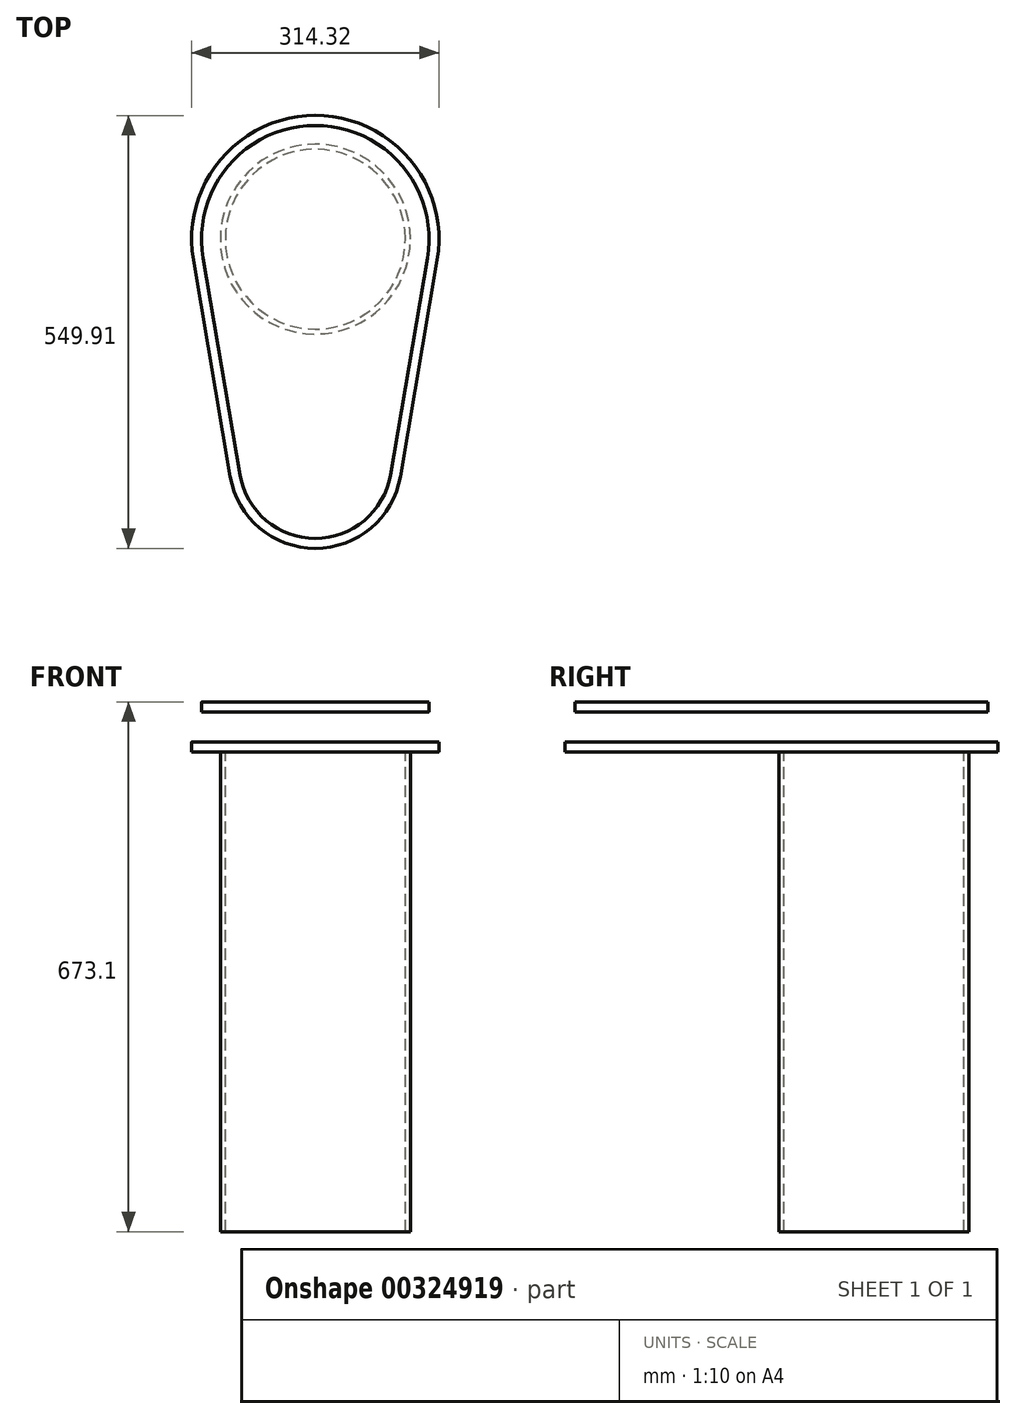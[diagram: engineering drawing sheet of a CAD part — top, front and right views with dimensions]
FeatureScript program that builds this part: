
annotation { "Feature Type Name" : "Feature", "Feature Type Description" : "" }
export const myFeature = defineFeature(function(context is Context, id is Id, definition is map)
    precondition{}
    {
        {
            var Q0;
            Q0=qCreatedBy(makeId("Top.planeOp"),FACE);
            var sketch = newSketch(context, id + "F0", { "sketchPlane" : qUnion([Q0])});
            skArc(sketch, "E0", {"start": v(142.4, -24.3) * mm, "mid": v(0, 144.46) * mm, "end": v(-142.4, -24.3) * mm});
            skArc(sketch, "E1", {"start": v(-95.46, -299.5) * mm, "mid": v(0, -380.05) * mm, "end": v(95.46, -299.5) * mm});
            skLineSegment(sketch, "E2", {"start": v(-142.4, -24.3) * mm, "end": v(-95.46, -299.5) * mm});
            skLineSegment(sketch, "E3", {"start": v(142.4, -24.3) * mm, "end": v(95.46, -299.5) * mm});
            skSolve(sketch);
        }
        {
            var Q0;
            Q0=qCreatedBy(makeId("Top.planeOp"),FACE);
            cPlane(context, id + "F1", {"entities" : qUnion([Q0]), "cplaneType" : CPlaneType.OFFSET, "offset" : 50.8 * mm, "oppositeDirection" : true, "width" : 152.4 * mm, "height" : 152.4 * mm});
        }
        {
            var Q0;
            Q0=qCreatedBy(id+"F1.planeOp",FACE);
            var sketch = newSketch(context, id + "F2", { "sketchPlane" : qUnion([Q0])});
            skLineSegment(sketch, "E4.0", {"start": v(-154.92, -26.43) * mm, "end": v(-107.98, -301.63) * mm});
            skArc(sketch, "E4.1", {"start": v(154.92, -26.43) * mm, "mid": v(0, 157.16) * mm, "end": v(-154.92, -26.43) * mm});
            skLineSegment(sketch, "E4.2", {"start": v(154.92, -26.43) * mm, "end": v(107.98, -301.63) * mm});
            skArc(sketch, "E4.3", {"start": v(-107.98, -301.63) * mm, "mid": v(0, -392.75) * mm, "end": v(107.98, -301.63) * mm});
            skSolve(sketch);
        }
        {
            var Q0;
            Q0=makeQuery(id+"F0.imprint","IMPRINT",FACE,{"disambiguationData":[TD([[makeQuery(id+"F0.imprint","IMPRINT",EDGE,{"derivedFrom":sQuery(id+"F0.wireOp",EDGE,"E0")}),1.0]])]});
            extrude(context, id + "F3", {"entities" : qUnion([Q0]), "oppositeDirection" : true, "depth" : 12.7 * mm});
        }
        {
            var Q0;
            Q0=makeQuery(id+"F2.imprint","IMPRINT",FACE,{"disambiguationData":[TD([[makeQuery(id+"F2.imprint","IMPRINT",EDGE,{"derivedFrom":sQuery(id+"F2.wireOp",EDGE,"E4.0")}),1.0]])]});
            extrude(context, id + "F4", {"entities" : qUnion([Q0]), "oppositeDirection" : true, "depth" : 12.7 * mm});
        }
        {
            var Q0;
            Q0=makeQuery(id+"F4.opExtrude","CAP_FACE",FACE,{"disambiguationData":[OSD([sQuery(id+"F2.wireOp",EDGE,"E4.0"),sQuery(id+"F2.wireOp",EDGE,"E4.1"),sQuery(id+"F2.wireOp",EDGE,"E4.2"),sQuery(id+"F2.wireOp",EDGE,"E4.3")])],"isStart":false});
            var sketch = newSketch(context, id + "F5", { "sketchPlane" : qUnion([Q0])});
            skCircle(sketch, "E5", {"center": v(0, 0) * mm, "radius": 114.3 * mm});
            skCircle(sketch, "E6.0", {"center": v(0, 0) * mm, "radius": 120.65 * mm});
            skSolve(sketch);
        }
        {
            var Q0;
            Q0=makeQuery(id+"F5.imprint","IMPRINT",FACE,{"disambiguationData":[TD([[makeQuery(id+"F5.imprint","IMPRINT",EDGE,{"derivedFrom":sQuery(id+"F5.wireOp",EDGE,"E5")}),-1.0]])]});
            extrude(context, id + "F6", {"entities" : qUnion([Q0]), "depth" : 609.6 * mm});
        }
    });
